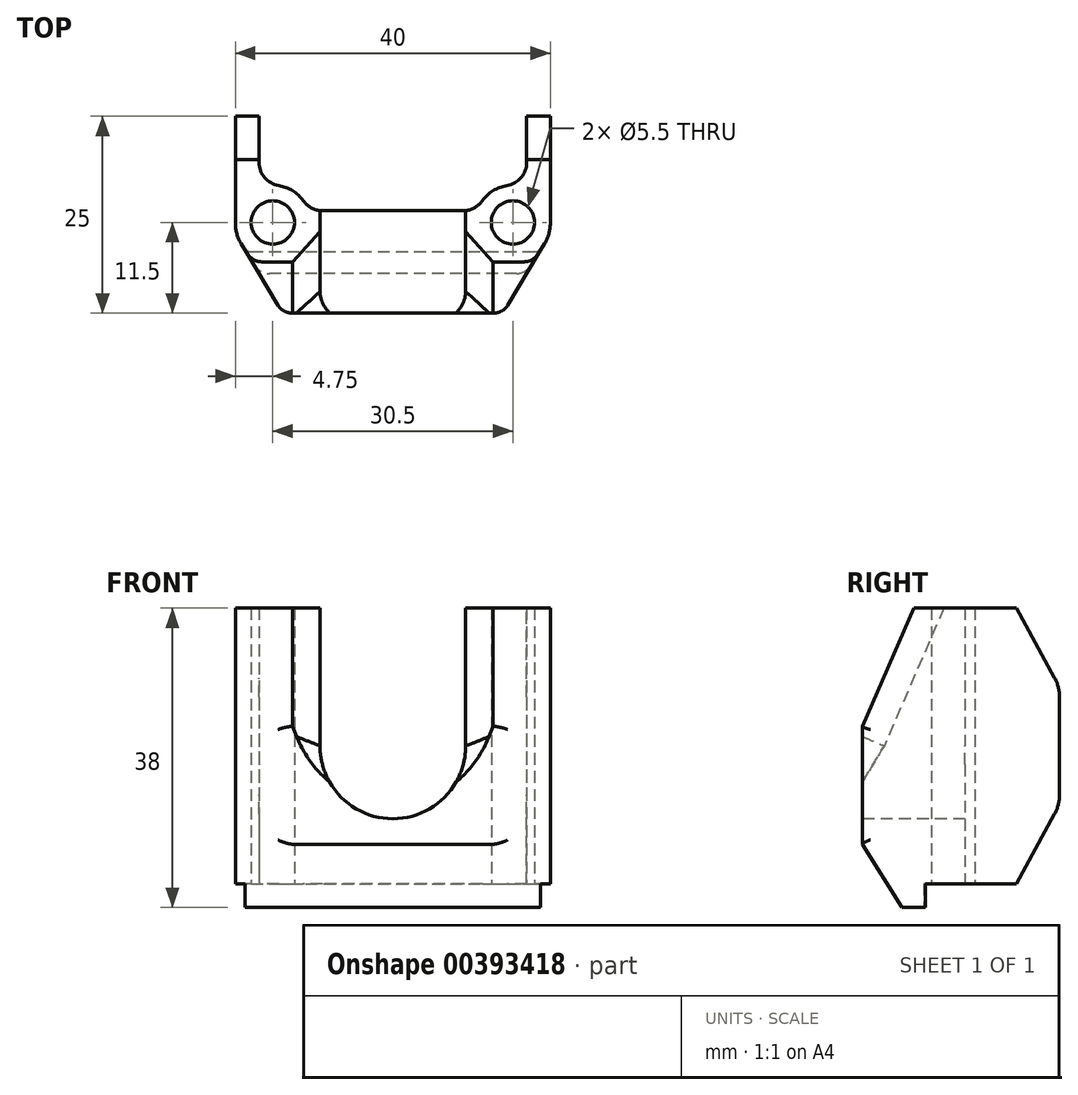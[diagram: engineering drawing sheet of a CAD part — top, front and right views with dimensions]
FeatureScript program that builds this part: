
annotation { "Feature Type Name" : "Feature", "Feature Type Description" : "" }
export const myFeature = defineFeature(function(context is Context, id is Id, definition is map)
    precondition{}
    {
        {
            var Q0;
            Q0=qCreatedBy(makeId("Top.planeOp"),FACE);
            var sketch = newSketch(context, id + "F0", { "sketchPlane" : qUnion([Q0])});
            skLineSegment(sketch, "E0.bottom", {"start": v(-20, 25) * mm, "end": v(-17, 25) * mm});
            skLineSegment(sketch, "E0.top", {"start": v(-20, 0) * mm, "end": v(20, 0) * mm});
            skLineSegment(sketch, "E0.left", {"start": v(-20, 25) * mm, "end": v(-20, 0) * mm});
            skLineSegment(sketch, "E1.top", {"start": v(-8.94, 13) * mm, "end": v(8.94, 13) * mm});
            skLineSegment(sketch, "E1.left", {"start": v(-17, 25) * mm, "end": v(-17, 19.15) * mm});
            skLineSegment(sketch, "E1.right", {"start": v(17, 25) * mm, "end": v(17, 19.15) * mm});
            skLineSegment(sketch, "E2.trimOffspring", {"start": v(17, 25) * mm, "end": v(20, 25) * mm});
            skCircle(sketch, "E3", {"center": v(-15.25, 11.5) * mm, "radius": 2.75 * mm});
            skCircle(sketch, "E4.MirrorC", {"center": v(15.25, 11.5) * mm, "radius": 2.75 * mm});
            skArc(sketch, "E5", {"start": v(-11.38, 14.26) * mm, "mid": v(-12.74, 15.53) * mm, "end": v(-14.48, 16.19) * mm});
            skArc(sketch, "E6.MirrorC", {"start": v(11.38, 14.26) * mm, "mid": v(12.74, 15.53) * mm, "end": v(14.48, 16.19) * mm});
            skPoint(sketch, "E7.visualSharp", {"position": v(-20, 0) * mm});
            skPoint(sketch, "E8.visualSharp", {"position": v(20, 0) * mm});
            skPoint(sketch, "E9.visualSharp", {"position": v(-17, 15.92) * mm});
            skArc(sketch, "E9.filletArc", {"start": v(-17, 19.15) * mm, "mid": v(-16.29, 17.2) * mm, "end": v(-14.48, 16.19) * mm});
            skPoint(sketch, "E10.visualSharp", {"position": v(-10.74, 13) * mm});
            skArc(sketch, "E10.filletArc", {"start": v(-11.38, 14.26) * mm, "mid": v(-10.31, 13.33) * mm, "end": v(-8.94, 13) * mm});
            skPoint(sketch, "E11.visualSharp", {"position": v(10.74, 13) * mm});
            skArc(sketch, "E11.filletArc", {"start": v(8.94, 13) * mm, "mid": v(10.31, 13.33) * mm, "end": v(11.38, 14.26) * mm});
            skPoint(sketch, "E12.visualSharp", {"position": v(17, 15.92) * mm});
            skArc(sketch, "E12.filletArc", {"start": v(14.48, 16.19) * mm, "mid": v(16.29, 17.2) * mm, "end": v(17, 19.15) * mm});
            skLineSegment(sketch, "E13.MirrorCS", {"start": v(20, 25) * mm, "end": v(20, 0) * mm});
            skSolve(sketch);
        }
        {
            var Q0;
            Q0=makeQuery(id+"F0.imprint","IMPRINT",FACE,{"disambiguationData":[TD([[makeQuery(id+"F0.imprint","IMPRINT",EDGE,{"derivedFrom":sQuery(id+"F0.wireOp",EDGE,"E0.bottom")}),-1.0]])]});
            extrude(context, id + "F1", {"entities" : qUnion([Q0]), "depth" : 38 * mm});
        }
        {
            var Q0;
            Q0=makeQuery(id+"F1.opExtrude","CAP_FACE",FACE,{"disambiguationData":[OSD([sQuery(id+"F0.wireOp",EDGE,"E0.bottom"),sQuery(id+"F0.wireOp",EDGE,"E0.top"),sQuery(id+"F0.wireOp",EDGE,"E0.left"),sQuery(id+"F0.wireOp",EDGE,"E1.top"),sQuery(id+"F0.wireOp",EDGE,"E1.left"),sQuery(id+"F0.wireOp",EDGE,"E1.right"),sQuery(id+"F0.wireOp",EDGE,"E2.trimOffspring"),sQuery(id+"F0.wireOp",EDGE,"E3"),sQuery(id+"F0.wireOp",EDGE,"E4.MirrorC"),sQuery(id+"F0.wireOp",EDGE,"E5"),sQuery(id+"F0.wireOp",EDGE,"E6.MirrorC"),sQuery(id+"F0.wireOp",EDGE,"E7.filletArc"),sQuery(id+"F0.wireOp",EDGE,"E8.filletArc"),sQuery(id+"F0.wireOp",EDGE,"E9.filletArc"),sQuery(id+"F0.wireOp",EDGE,"E10.filletArc"),sQuery(id+"F0.wireOp",EDGE,"E11.filletArc"),sQuery(id+"F0.wireOp",EDGE,"E12.filletArc"),sQuery(id+"F0.wireOp",EDGE,"WYs83tg2-3YYL-TYyd-ICu3-mPrBzIMUOPxt.left"),sQuery(id+"F0.wireOp",EDGE,"5Hqr8FUe-WFyd-d302-SElr-T4tz6ILiSn6Z"),sQuery(id+"F0.wireOp",EDGE,"ccd3453e-2388-4469-8aed-a6895ced8886.filletArc"),sQuery(id+"F0.wireOp",EDGE,"02acf525-3c1e-4234-b231-e13aca6db888.filletArc"),sQuery(id+"F0.wireOp",EDGE,"842c10dc-a033-4d9a-a338-8859e4b5ca2d0.MirrorCS"),sQuery(id+"F0.wireOp",EDGE,"92a6c8df-cb0f-405c-93f6-13e0b38793100.MirrorCS"),sQuery(id+"F0.wireOp",EDGE,"025cc89f-8fe4-4bd3-b1ee-0f33fe3694280.MirrorCS"),sQuery(id+"F0.wireOp",EDGE,"679e2703-3c45-41c1-998c-2d78e486eee40.MirrorCS"),sQuery(id+"F0.wireOp",EDGE,"E13.MirrorCS")])],"isStart":true});
            var sketch = newSketch(context, id + "F2", { "sketchPlane" : qUnion([Q0])});
            skLineSegment(sketch, "E14.bottom", {"start": v(-18, -7.8) * mm, "end": v(18, -7.8) * mm});
            skLineSegment(sketch, "E14.top", {"start": v(-20, -60) * mm, "end": v(20, -60) * mm});
            skLineSegment(sketch, "E14.left", {"start": v(-20, -9.8) * mm, "end": v(-20, -60) * mm});
            skLineSegment(sketch, "E14.right", {"start": v(20, -9.8) * mm, "end": v(20, -60) * mm});
            skPoint(sketch, "E15.visualSharp", {"position": v(-20, -7.8) * mm});
            skArc(sketch, "E15.filletArc", {"start": v(-18, -7.8) * mm, "mid": v(-19.41, -8.39) * mm, "end": v(-20, -9.8) * mm});
            skPoint(sketch, "E16.visualSharp", {"position": v(20, -7.8) * mm});
            skArc(sketch, "E16.filletArc", {"start": v(20, -9.8) * mm, "mid": v(19.41, -8.39) * mm, "end": v(18, -7.8) * mm});
            skSolve(sketch);
        }
        {
            var Q0;
            Q0 = qSketchRegion(id + "F2", true);
            extrude(context, id + "F3", {"entities" : qUnion([Q0]), "operationType" : NewBodyOperationType.REMOVE, "oppositeDirection" : true, "depth" : 3 * mm});
        }
        {
            var Q0;
            Q0=makeQuery(id+"F1.opExtrude","SWEPT_FACE",FACE,{"disambiguationData":[OSD([sQuery(id+"F0.wireOp",EDGE,"E0.top")])]});
            var sketch = newSketch(context, id + "F4", { "sketchPlane" : qUnion([Q0])});
            skArc(sketch, "E17", {"start": v(-9.25, 20.5) * mm, "mid": v(0, 11.25) * mm, "end": v(9.25, 20.5) * mm});
            skLineSegment(sketch, "E18", {"start": v(-9.25, 20.5) * mm, "end": v(-9.25, 38) * mm});
            skLineSegment(sketch, "E19", {"start": v(9.25, 20.5) * mm, "end": v(9.25, 38) * mm});
            skLineSegment(sketch, "E20", {"start": v(9.25, 38) * mm, "end": v(-9.25, 38) * mm});
            skSolve(sketch);
        }
        {
            var Q0;
            Q0=makeQuery(id+"F4.imprint","IMPRINT",FACE,{"disambiguationData":[TD([[makeQuery(id+"F4.imprint","IMPRINT",EDGE,{"derivedFrom":sQuery(id+"F4.wireOp",EDGE,"E17")}),1.0]])]});
            extrude(context, id + "F5", {"entities" : qUnion([Q0]), "operationType" : NewBodyOperationType.REMOVE, "oppositeDirection" : true, "depth" : 25 * mm});
        }
        {
            var Q0;
            Q0=makeQuery(id+"F1.opExtrude","CAP_EDGE",EDGE,{"disambiguationData":[OSD([sQuery(id+"F0.wireOp",EDGE,"E0.top")])],"isStart":true});
            chamfer(context, id + "F6", {"entities" : qUnion([Q0]), "chamferType" : ChamferType.TWO_OFFSETS, "width1" : 8 * mm, "oppositeDirection" : false, "width2" : 5 * mm, "tangentPropagation" : true});
        }
        {
            var Q0;
            {var subQ0=sQuery(id+"F0.wireOp",EDGE,"E0.left");var subQ1=sQuery(id+"F0.wireOp",EDGE,"E0.top");Q0=makeQuery(id+"F5.boolean.opBoolean","SPLIT",EDGE,{"disambiguationData":[TD([makeQuery(id+"F1.opExtrude","SWEPT_FACE",FACE,{"disambiguationData":[OSD([subQ0])]})])],"derivedFrom":makeQuery(id+"F1.opExtrude","CAP_EDGE",EDGE,{"disambiguationData":[OSD([subQ1])],"isStart":false})});}
            var Q1;
            {var subQ0=sQuery(id+"F0.wireOp",EDGE,"E13.MirrorCS");var subQ1=sQuery(id+"F0.wireOp",EDGE,"E0.top");Q1=makeQuery(id+"F5.boolean.opBoolean","SPLIT",EDGE,{"disambiguationData":[TD([makeQuery(id+"F1.opExtrude","SWEPT_FACE",FACE,{"disambiguationData":[OSD([subQ0])]})])],"derivedFrom":makeQuery(id+"F1.opExtrude","CAP_EDGE",EDGE,{"disambiguationData":[OSD([subQ1])],"isStart":false})});}
            chamfer(context, id + "F7", {"entities" : qUnion([Q0, Q1]), "chamferType" : ChamferType.TWO_OFFSETS, "width1" : 6.5 * mm, "oppositeDirection" : false, "width2" : 15 * mm});
        }
        {
            var Q0;
            Q0=makeQuery(id+"F1.opExtrude","SWEPT_EDGE",EDGE,{"disambiguationData":[OSD([sQuery(id+"F0.wireOp",EDGE,"E0.top"),sQuery(id+"F0.wireOp",EDGE,"E13.MirrorCS")])]});
            chamfer(context, id + "F8", {"entities" : qUnion([Q0]), "chamferType" : ChamferType.TWO_OFFSETS, "width1" : 10 * mm, "oppositeDirection" : false, "width2" : 6 * mm, "tangentPropagation" : true});
        }
        {
            var Q0;
            Q0=makeQuery(id+"F1.opExtrude","SWEPT_EDGE",EDGE,{"disambiguationData":[OSD([sQuery(id+"F0.wireOp",EDGE,"E0.top"),sQuery(id+"F0.wireOp",EDGE,"E0.left")])]});
            chamfer(context, id + "F9", {"entities" : qUnion([Q0]), "chamferType" : ChamferType.TWO_OFFSETS, "width1" : 6 * mm, "oppositeDirection" : false, "width2" : 10 * mm, "tangentPropagation" : true});
        }
        {
            var Q0;
            {var subQ0=sQuery(id+"F0.wireOp",EDGE,"E13.MirrorCS");var subQ1=sQuery(id+"F0.wireOp",EDGE,"E0.top");Q0=makeQuery(id+"F8.opChamfer","BLEND_EDGE",EDGE,{"blendedFrom":[makeQuery(id+"F1.opExtrude","SWEPT_EDGE",EDGE,{"disambiguationData":[OSD([subQ1,subQ0])]}),makeQuery(id+"F7.opChamfer","BLEND_FACE",FACE,{"disambiguationData":[OSD([subQ1]),TDD([makeQuery(id+"F5.boolean.opBoolean","SPLIT",EDGE,{"disambiguationData":[TD([makeQuery(id+"F1.opExtrude","SWEPT_FACE",FACE,{"disambiguationData":[OSD([subQ0])]})])],"derivedFrom":makeQuery(id+"F1.opExtrude","CAP_EDGE",EDGE,{"disambiguationData":[OSD([subQ1])],"isStart":false})})])]})],"blendedInto":[makeQuery(id+"F7.opChamfer","BLEND_FACE",FACE,{"disambiguationData":[OSD([subQ1]),TDD([makeQuery(id+"F5.boolean.opBoolean","SPLIT",EDGE,{"disambiguationData":[TD([makeQuery(id+"F1.opExtrude","SWEPT_FACE",FACE,{"disambiguationData":[OSD([subQ0])]})])],"derivedFrom":makeQuery(id+"F1.opExtrude","CAP_EDGE",EDGE,{"disambiguationData":[OSD([subQ1])],"isStart":false})})])]})]});}
            var Q1;
            {var subQ0=sQuery(id+"F0.wireOp",EDGE,"E0.left");var subQ1=sQuery(id+"F0.wireOp",EDGE,"E0.top");Q1=makeQuery(id+"F9.opChamfer","BLEND_EDGE",EDGE,{"blendedFrom":[makeQuery(id+"F1.opExtrude","SWEPT_EDGE",EDGE,{"disambiguationData":[OSD([subQ1,subQ0])]}),makeQuery(id+"F7.opChamfer","BLEND_FACE",FACE,{"disambiguationData":[OSD([subQ1]),TDD([makeQuery(id+"F5.boolean.opBoolean","SPLIT",EDGE,{"disambiguationData":[TD([makeQuery(id+"F1.opExtrude","SWEPT_FACE",FACE,{"disambiguationData":[OSD([subQ0])]})])],"derivedFrom":makeQuery(id+"F1.opExtrude","CAP_EDGE",EDGE,{"disambiguationData":[OSD([subQ1])],"isStart":false})})])]})],"blendedInto":[makeQuery(id+"F7.opChamfer","BLEND_FACE",FACE,{"disambiguationData":[OSD([subQ1]),TDD([makeQuery(id+"F5.boolean.opBoolean","SPLIT",EDGE,{"disambiguationData":[TD([makeQuery(id+"F1.opExtrude","SWEPT_FACE",FACE,{"disambiguationData":[OSD([subQ0])]})])],"derivedFrom":makeQuery(id+"F1.opExtrude","CAP_EDGE",EDGE,{"disambiguationData":[OSD([subQ1])],"isStart":false})})])]})]});}
            var Q2;
            {var subQ0=sQuery(id+"F0.wireOp",EDGE,"E0.top");Q2=makeQuery(id+"F8.opChamfer","BLEND_EDGE",EDGE,{"blendedFrom":[makeQuery(id+"F1.opExtrude","SWEPT_EDGE",EDGE,{"disambiguationData":[OSD([subQ0,sQuery(id+"F0.wireOp",EDGE,"E13.MirrorCS")])]}),makeQuery(id+"F1.opExtrude","SWEPT_FACE",FACE,{"disambiguationData":[OSD([subQ0])]})],"blendedInto":[makeQuery(id+"F1.opExtrude","SWEPT_FACE",FACE,{"disambiguationData":[OSD([subQ0])]})]});}
            var Q3;
            {var subQ0=sQuery(id+"F0.wireOp",EDGE,"E0.top");Q3=makeQuery(id+"F9.opChamfer","BLEND_EDGE",EDGE,{"blendedFrom":[makeQuery(id+"F1.opExtrude","SWEPT_EDGE",EDGE,{"disambiguationData":[OSD([subQ0,sQuery(id+"F0.wireOp",EDGE,"E0.left")])]}),makeQuery(id+"F1.opExtrude","SWEPT_FACE",FACE,{"disambiguationData":[OSD([subQ0])]})],"blendedInto":[makeQuery(id+"F1.opExtrude","SWEPT_FACE",FACE,{"disambiguationData":[OSD([subQ0])]})]});}
            var Q4;
            {var subQ0=sQuery(id+"F0.wireOp",EDGE,"E0.top");Q4=makeQuery(id+"F9.opChamfer","BLEND_EDGE",EDGE,{"blendedFrom":[makeQuery(id+"F1.opExtrude","SWEPT_EDGE",EDGE,{"disambiguationData":[OSD([subQ0,sQuery(id+"F0.wireOp",EDGE,"E0.left")])]}),makeQuery(id+"F6.opChamfer","BLEND_FACE",FACE,{"disambiguationData":[OSD([subQ0])]})],"blendedInto":[makeQuery(id+"F6.opChamfer","BLEND_FACE",FACE,{"disambiguationData":[OSD([subQ0])]})]});}
            var Q5;
            {var subQ0=sQuery(id+"F0.wireOp",EDGE,"E0.top");Q5=makeQuery(id+"F8.opChamfer","BLEND_EDGE",EDGE,{"blendedFrom":[makeQuery(id+"F1.opExtrude","SWEPT_EDGE",EDGE,{"disambiguationData":[OSD([subQ0,sQuery(id+"F0.wireOp",EDGE,"E13.MirrorCS")])]}),makeQuery(id+"F6.opChamfer","BLEND_FACE",FACE,{"disambiguationData":[OSD([subQ0])]})],"blendedInto":[makeQuery(id+"F6.opChamfer","BLEND_FACE",FACE,{"disambiguationData":[OSD([subQ0])]})]});}
            fillet(context, id + "F10", {"entities" : qUnion([Q0, Q1, Q2, Q3, Q4, Q5]), "radius" : 2 * mm, "tangentPropagation" : true, "allowEdgeOverflow" : false});
        }
        {
            var Q0;
            Q0=makeQuery(id+"F3.boolean.opBoolean","INTERSECT",EDGE,{"derivedFrom":[makeQuery(id+"F1.opExtrude","SWEPT_FACE",FACE,{"disambiguationData":[OSD([sQuery(id+"F0.wireOp",EDGE,"E2.trimOffspring")])]}),makeQuery(id+"F3.opExtrude","CAP_FACE",FACE,{"disambiguationData":[OSD([sQuery(id+"F2.wireOp",EDGE,"E14.bottom"),sQuery(id+"F2.wireOp",EDGE,"E14.top"),sQuery(id+"F2.wireOp",EDGE,"E14.left"),sQuery(id+"F2.wireOp",EDGE,"E14.right"),sQuery(id+"F2.wireOp",EDGE,"E15.filletArc"),sQuery(id+"F2.wireOp",EDGE,"E16.filletArc")])],"isStart":false})]});
            var Q1;
            Q1=makeQuery(id+"F3.boolean.opBoolean","INTERSECT",EDGE,{"derivedFrom":[makeQuery(id+"F1.opExtrude","SWEPT_FACE",FACE,{"disambiguationData":[OSD([sQuery(id+"F0.wireOp",EDGE,"E0.bottom")])]}),makeQuery(id+"F3.opExtrude","CAP_FACE",FACE,{"disambiguationData":[OSD([sQuery(id+"F2.wireOp",EDGE,"E14.bottom"),sQuery(id+"F2.wireOp",EDGE,"E14.top"),sQuery(id+"F2.wireOp",EDGE,"E14.left"),sQuery(id+"F2.wireOp",EDGE,"E14.right"),sQuery(id+"F2.wireOp",EDGE,"E15.filletArc"),sQuery(id+"F2.wireOp",EDGE,"E16.filletArc")])],"isStart":false})]});
            chamfer(context, id + "F11", {"entities" : qUnion([Q0, Q1]), "chamferType" : ChamferType.TWO_OFFSETS, "width1" : 10 * mm, "oppositeDirection" : false, "width2" : 5.5 * mm, "tangentPropagation" : true});
        }
        {
            var Q0;
            Q0=makeQuery(id+"F1.opExtrude","CAP_EDGE",EDGE,{"disambiguationData":[OSD([sQuery(id+"F0.wireOp",EDGE,"E2.trimOffspring")])],"isStart":false});
            var Q1;
            Q1=makeQuery(id+"F1.opExtrude","CAP_EDGE",EDGE,{"disambiguationData":[OSD([sQuery(id+"F0.wireOp",EDGE,"E0.bottom")])],"isStart":false});
            chamfer(context, id + "F12", {"entities" : qUnion([Q0, Q1]), "chamferType" : ChamferType.TWO_OFFSETS, "width1" : 10 * mm, "oppositeDirection" : false, "width2" : 5.5 * mm, "tangentPropagation" : true});
        }
        {
            var Q0;
            {var subQ0=sQuery(id+"F0.wireOp",EDGE,"E13.MirrorCS");Q0=makeQuery(id+"F8.opChamfer","BLEND_EDGE",EDGE,{"blendedFrom":[makeQuery(id+"F1.opExtrude","SWEPT_EDGE",EDGE,{"disambiguationData":[OSD([sQuery(id+"F0.wireOp",EDGE,"E0.top"),subQ0])]}),makeQuery(id+"F1.opExtrude","SWEPT_FACE",FACE,{"disambiguationData":[OSD([subQ0])]})],"blendedInto":[makeQuery(id+"F1.opExtrude","SWEPT_FACE",FACE,{"disambiguationData":[OSD([subQ0])]})]});}
            var Q1;
            {var subQ0=sQuery(id+"F0.wireOp",EDGE,"E0.left");Q1=makeQuery(id+"F9.opChamfer","BLEND_EDGE",EDGE,{"blendedFrom":[makeQuery(id+"F1.opExtrude","SWEPT_EDGE",EDGE,{"disambiguationData":[OSD([sQuery(id+"F0.wireOp",EDGE,"E0.top"),subQ0])]}),makeQuery(id+"F1.opExtrude","SWEPT_FACE",FACE,{"disambiguationData":[OSD([subQ0])]})],"blendedInto":[makeQuery(id+"F1.opExtrude","SWEPT_FACE",FACE,{"disambiguationData":[OSD([subQ0])]})]});}
            fillet(context, id + "F13", {"entities" : qUnion([Q0, Q1]), "radius" : 5 * mm, "tangentPropagation" : true, "allowEdgeOverflow" : false});
        }
        {
            var Q0;
            {var subQ0=sQuery(id+"F0.wireOp",EDGE,"E2.trimOffspring");Q0=makeQuery(id+"F12.opChamfer","BLEND_EDGE",EDGE,{"blendedFrom":[makeQuery(id+"F1.opExtrude","CAP_EDGE",EDGE,{"disambiguationData":[OSD([subQ0])],"isStart":false}),makeQuery(id+"F1.opExtrude","SWEPT_FACE",FACE,{"disambiguationData":[OSD([subQ0])]})],"blendedInto":[makeQuery(id+"F1.opExtrude","SWEPT_FACE",FACE,{"disambiguationData":[OSD([subQ0])]})]});}
            var Q1;
            {var subQ0=makeQuery(id+"F1.opExtrude","SWEPT_FACE",FACE,{"disambiguationData":[OSD([sQuery(id+"F0.wireOp",EDGE,"E2.trimOffspring")])]});Q1=makeQuery(id+"F11.opChamfer","BLEND_EDGE",EDGE,{"blendedFrom":[makeQuery(id+"F3.boolean.opBoolean","INTERSECT",EDGE,{"derivedFrom":[subQ0,makeQuery(id+"F3.opExtrude","CAP_FACE",FACE,{"disambiguationData":[OSD([sQuery(id+"F2.wireOp",EDGE,"E14.bottom"),sQuery(id+"F2.wireOp",EDGE,"E14.top"),sQuery(id+"F2.wireOp",EDGE,"E14.left"),sQuery(id+"F2.wireOp",EDGE,"E14.right"),sQuery(id+"F2.wireOp",EDGE,"E15.filletArc"),sQuery(id+"F2.wireOp",EDGE,"E16.filletArc")])],"isStart":false})]}),subQ0],"blendedInto":[subQ0]});}
            var Q2;
            {var subQ0=makeQuery(id+"F1.opExtrude","SWEPT_FACE",FACE,{"disambiguationData":[OSD([sQuery(id+"F0.wireOp",EDGE,"E0.bottom")])]});Q2=makeQuery(id+"F11.opChamfer","BLEND_EDGE",EDGE,{"blendedFrom":[makeQuery(id+"F3.boolean.opBoolean","INTERSECT",EDGE,{"derivedFrom":[subQ0,makeQuery(id+"F3.opExtrude","CAP_FACE",FACE,{"disambiguationData":[OSD([sQuery(id+"F2.wireOp",EDGE,"E14.bottom"),sQuery(id+"F2.wireOp",EDGE,"E14.top"),sQuery(id+"F2.wireOp",EDGE,"E14.left"),sQuery(id+"F2.wireOp",EDGE,"E14.right"),sQuery(id+"F2.wireOp",EDGE,"E15.filletArc"),sQuery(id+"F2.wireOp",EDGE,"E16.filletArc")])],"isStart":false})]}),subQ0],"blendedInto":[subQ0]});}
            var Q3;
            {var subQ0=sQuery(id+"F0.wireOp",EDGE,"E0.bottom");Q3=makeQuery(id+"F12.opChamfer","BLEND_EDGE",EDGE,{"blendedFrom":[makeQuery(id+"F1.opExtrude","CAP_EDGE",EDGE,{"disambiguationData":[OSD([subQ0])],"isStart":false}),makeQuery(id+"F1.opExtrude","SWEPT_FACE",FACE,{"disambiguationData":[OSD([subQ0])]})],"blendedInto":[makeQuery(id+"F1.opExtrude","SWEPT_FACE",FACE,{"disambiguationData":[OSD([subQ0])]})]});}
            fillet(context, id + "F14", {"entities" : qUnion([Q0, Q1, Q2, Q3]), "radius" : 5 * mm, "tangentPropagation" : true, "allowEdgeOverflow" : false});
        }
        {
            var Q0;
            {var subQ0=makeQuery(id+"F5.opExtrude","SWEPT_FACE",FACE,{"disambiguationData":[OSD([sQuery(id+"F4.wireOp",EDGE,"E18")])]});var subQ1=sQuery(id+"F0.wireOp",EDGE,"E0.left");var subQ2=sQuery(id+"F0.wireOp",EDGE,"E0.top");Q0=makeQuery(id+"F7.opChamfer","BLEND_EDGE",EDGE,{"blendedFrom":[makeQuery(id+"F5.boolean.opBoolean","SPLIT",EDGE,{"disambiguationData":[TD([makeQuery(id+"F1.opExtrude","SWEPT_FACE",FACE,{"disambiguationData":[OSD([subQ1])]})])],"derivedFrom":makeQuery(id+"F1.opExtrude","CAP_EDGE",EDGE,{"disambiguationData":[OSD([subQ2])],"isStart":false})}),makeQuery(id+"F5.boolean.opBoolean","COPY",FACE,{"derivedFrom":subQ0})],"blendedInto":[makeQuery(id+"F5.boolean.opBoolean","COPY",FACE,{"derivedFrom":subQ0})]});}
            var Q1;
            {var subQ0=makeQuery(id+"F5.opExtrude","SWEPT_FACE",FACE,{"disambiguationData":[OSD([sQuery(id+"F4.wireOp",EDGE,"E18")])]});var subQ1=sQuery(id+"F0.wireOp",EDGE,"E0.top");var subQ2=makeQuery(id+"F1.opExtrude","SWEPT_FACE",FACE,{"disambiguationData":[OSD([subQ1])]});var subQ3=sQuery(id+"F0.wireOp",EDGE,"E0.left");Q1=makeQuery(id+"F10.opFillet","BLEND_EDGE",EDGE,{"blendedFrom":[makeQuery(id+"F7.opChamfer","BLEND_EDGE",EDGE,{"blendedFrom":[makeQuery(id+"F5.boolean.opBoolean","SPLIT",EDGE,{"disambiguationData":[TD([makeQuery(id+"F1.opExtrude","SWEPT_FACE",FACE,{"disambiguationData":[OSD([subQ3])]})])],"derivedFrom":makeQuery(id+"F1.opExtrude","CAP_EDGE",EDGE,{"disambiguationData":[OSD([subQ1])],"isStart":false})}),subQ2],"blendedInto":[subQ2]}),makeQuery(id+"F5.boolean.opBoolean","COPY",FACE,{"derivedFrom":subQ0})],"blendedInto":[makeQuery(id+"F5.boolean.opBoolean","COPY",FACE,{"derivedFrom":subQ0})]});}
            var Q2;
            Q2=makeQuery(id+"F5.boolean.opBoolean","COPY",EDGE,{"derivedFrom":makeQuery(id+"F5.opExtrude","CAP_EDGE",EDGE,{"disambiguationData":[OSD([sQuery(id+"F4.wireOp",EDGE,"E18")])],"isStart":true})});
            var Q3;
            Q3=makeQuery(id+"F5.boolean.opBoolean","COPY",EDGE,{"derivedFrom":makeQuery(id+"F5.opExtrude","CAP_EDGE",EDGE,{"disambiguationData":[OSD([sQuery(id+"F4.wireOp",EDGE,"E17")])],"isStart":true})});
            var Q4;
            {var subQ0=makeQuery(id+"F5.opExtrude","SWEPT_FACE",FACE,{"disambiguationData":[OSD([sQuery(id+"F4.wireOp",EDGE,"E19")])]});var subQ1=sQuery(id+"F0.wireOp",EDGE,"E0.top");var subQ2=makeQuery(id+"F1.opExtrude","SWEPT_FACE",FACE,{"disambiguationData":[OSD([subQ1])]});var subQ3=sQuery(id+"F0.wireOp",EDGE,"E13.MirrorCS");Q4=makeQuery(id+"F10.opFillet","BLEND_EDGE",EDGE,{"blendedFrom":[makeQuery(id+"F7.opChamfer","BLEND_EDGE",EDGE,{"blendedFrom":[makeQuery(id+"F5.boolean.opBoolean","SPLIT",EDGE,{"disambiguationData":[TD([makeQuery(id+"F1.opExtrude","SWEPT_FACE",FACE,{"disambiguationData":[OSD([subQ3])]})])],"derivedFrom":makeQuery(id+"F1.opExtrude","CAP_EDGE",EDGE,{"disambiguationData":[OSD([subQ1])],"isStart":false})}),subQ2],"blendedInto":[subQ2]}),makeQuery(id+"F5.boolean.opBoolean","COPY",FACE,{"derivedFrom":subQ0})],"blendedInto":[makeQuery(id+"F5.boolean.opBoolean","COPY",FACE,{"derivedFrom":subQ0})]});}
            var Q5;
            Q5=makeQuery(id+"F5.boolean.opBoolean","COPY",EDGE,{"derivedFrom":makeQuery(id+"F5.opExtrude","CAP_EDGE",EDGE,{"disambiguationData":[OSD([sQuery(id+"F4.wireOp",EDGE,"E19")])],"isStart":true})});
            var Q6;
            {var subQ0=makeQuery(id+"F5.opExtrude","SWEPT_FACE",FACE,{"disambiguationData":[OSD([sQuery(id+"F4.wireOp",EDGE,"E19")])]});var subQ1=sQuery(id+"F0.wireOp",EDGE,"E13.MirrorCS");var subQ2=sQuery(id+"F0.wireOp",EDGE,"E0.top");Q6=makeQuery(id+"F7.opChamfer","BLEND_EDGE",EDGE,{"blendedFrom":[makeQuery(id+"F5.boolean.opBoolean","SPLIT",EDGE,{"disambiguationData":[TD([makeQuery(id+"F1.opExtrude","SWEPT_FACE",FACE,{"disambiguationData":[OSD([subQ1])]})])],"derivedFrom":makeQuery(id+"F1.opExtrude","CAP_EDGE",EDGE,{"disambiguationData":[OSD([subQ2])],"isStart":false})}),makeQuery(id+"F5.boolean.opBoolean","COPY",FACE,{"derivedFrom":subQ0})],"blendedInto":[makeQuery(id+"F5.boolean.opBoolean","COPY",FACE,{"derivedFrom":subQ0})]});}
            chamfer(context, id + "F15", {"entities" : qUnion([Q0, Q1, Q2, Q3, Q4, Q5, Q6]), "width" : 3.5 * mm, "tangentPropagation" : true});
        }
    });
